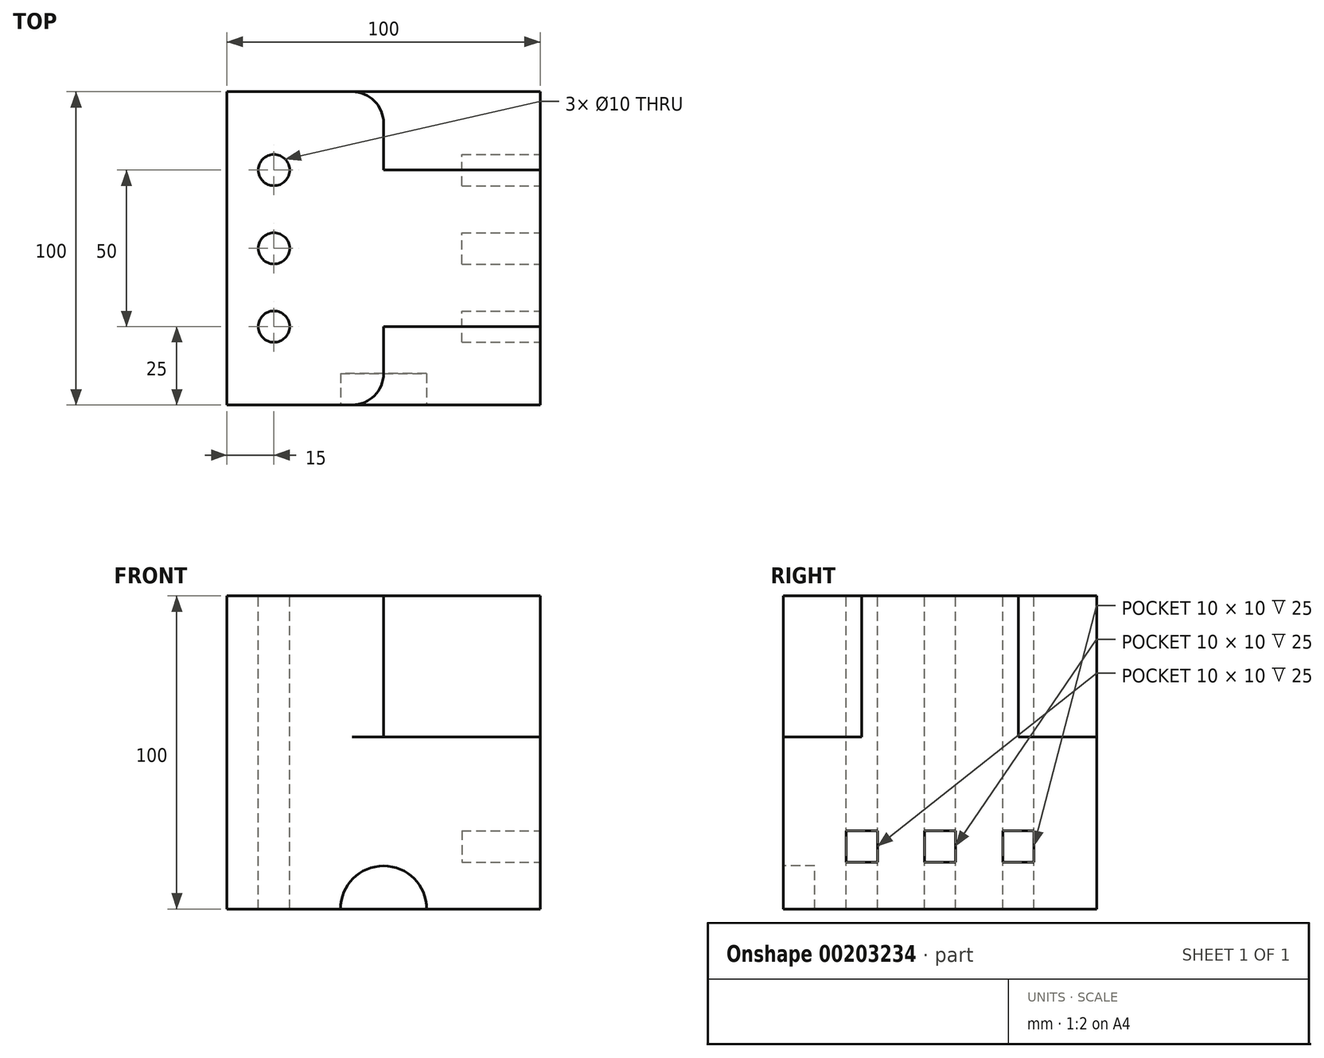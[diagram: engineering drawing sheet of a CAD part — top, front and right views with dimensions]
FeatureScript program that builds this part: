
annotation { "Feature Type Name" : "Feature", "Feature Type Description" : "" }
export const myFeature = defineFeature(function(context is Context, id is Id, definition is map)
    precondition{}
    {
        {
            var Q0;
            Q0=qCreatedBy(makeId("Front.planeOp"),FACE);
            var sketch = newSketch(context, id + "F0", { "sketchPlane" : qUnion([Q0])});
            skLineSegment(sketch, "E0", {"start": v(0, 0) * mm, "end": v(100, 0) * mm});
            skLineSegment(sketch, "E1", {"start": v(100, 0) * mm, "end": v(100, 100) * mm});
            skLineSegment(sketch, "E2", {"start": v(100, 100) * mm, "end": v(0, 100) * mm});
            skLineSegment(sketch, "E3", {"start": v(0, 100) * mm, "end": v(0, 0) * mm});
            skSolve(sketch);
        }
        {
            var Q0;
            Q0=makeQuery(id+"F0.imprint","IMPRINT",FACE,{"disambiguationData":[TD([[makeQuery(id+"F0.imprint","IMPRINT",EDGE,{"derivedFrom":sQuery(id+"F0.wireOp",EDGE,"E0")}),1.0]])]});
            extrude(context, id + "F1", {"entities" : qUnion([Q0]), "depth" : 100 * mm});
        }
        {
            var Q0;
            Q0=makeQuery(id+"F1.opExtrude","SWEPT_FACE",FACE,{"disambiguationData":[OSD([sQuery(id+"F0.wireOp",EDGE,"E2")])]});
            var sketch = newSketch(context, id + "F2", { "sketchPlane" : qUnion([Q0])});
            skLineSegment(sketch, "E4", {"start": v(100, -25) * mm, "end": v(50, -25) * mm});
            skLineSegment(sketch, "E5", {"start": v(50, -10) * mm, "end": v(50, -25) * mm});
            skLineSegment(sketch, "E6", {"start": v(50, -75) * mm, "end": v(100, -75) * mm});
            skLineSegment(sketch, "E7", {"start": v(50, -75) * mm, "end": v(50, -90) * mm});
            skLineSegment(sketch, "E8", {"start": v(0, -100) * mm, "end": v(40, -100) * mm});
            skPoint(sketch, "E9.visualSharp", {"position": v(50, -100) * mm});
            skArc(sketch, "E9.filletArc", {"start": v(40, -100) * mm, "mid": v(47.07, -97.07) * mm, "end": v(50, -90) * mm});
            skLineSegment(sketch, "E10", {"start": v(40, 0) * mm, "end": v(15.8, 0) * mm});
            skLineSegment(sketch, "E11", {"start": v(100, -25) * mm, "end": v(100, -75) * mm});
            skPoint(sketch, "E12.visualSharp", {"position": v(50, 0) * mm});
            skArc(sketch, "E12.filletArc", {"start": v(50, -10) * mm, "mid": v(47.07, -2.93) * mm, "end": v(40, 0) * mm});
            skCircle(sketch, "E13", {"center": v(15, -25) * mm, "radius": 5 * mm});
            skCircle(sketch, "E14", {"center": v(15, -50) * mm, "radius": 5 * mm});
            skCircle(sketch, "E15", {"center": v(15, -75) * mm, "radius": 5 * mm});
            skSolve(sketch);
        }
        {
            var Q0;
            Q0=makeQuery(id+"F2.imprint","IMPRINT",FACE,{"disambiguationData":[TD([[makeQuery(id+"F2.imprint","IMPRINT",EDGE,{"derivedFrom":sQuery(id+"F2.wireOp",EDGE,"E13")}),1.0]])]});
            var Q1;
            Q1=makeQuery(id+"F2.imprint","IMPRINT",FACE,{"disambiguationData":[TD([[makeQuery(id+"F2.imprint","IMPRINT",EDGE,{"derivedFrom":sQuery(id+"F2.wireOp",EDGE,"E14")}),1.0]])]});
            var Q2;
            Q2=makeQuery(id+"F2.imprint","IMPRINT",FACE,{"disambiguationData":[TD([[makeQuery(id+"F2.imprint","IMPRINT",EDGE,{"derivedFrom":sQuery(id+"F2.wireOp",EDGE,"E15")}),1.0]])]});
            var Q3;
            Q3=sQuery(id+"F2.wireOp",EDGE,"E13");
            var Q4;
            Q4=sQuery(id+"F2.wireOp",EDGE,"E14");
            var Q5;
            Q5=sQuery(id+"F2.wireOp",EDGE,"E15");
            extrude(context, id + "F3", {"entities" : qUnion([Q0, Q1, Q2]), "operationType" : NewBodyOperationType.REMOVE, "surfaceEntities" : qUnion([Q3, Q4, Q5]), "endBound" : BoundingType.THROUGH_ALL, "oppositeDirection" : true, "depth" : 25 * mm});
        }
        {
            var Q0;
            {var subQ4=sQuery(id+"F2.wireOp",EDGE,"E4");Q0=makeQuery(id+"F2.imprint","IMPRINT",FACE,{"disambiguationData":[TD([[makeQuery(id+"F2.imprint","IMPRINT",EDGE,{"derivedFrom":subQ4}),-1.0]])]});}
            var Q1;
            {var subQ5=sQuery(id+"F2.wireOp",EDGE,"E6");Q1=makeQuery(id+"F2.imprint","IMPRINT",FACE,{"disambiguationData":[TD([[makeQuery(id+"F2.imprint","IMPRINT",EDGE,{"derivedFrom":subQ5}),-1.0]])]});}
            extrude(context, id + "F4", {"entities" : qUnion([Q0, Q1]), "operationType" : NewBodyOperationType.REMOVE, "oppositeDirection" : true, "depth" : 45 * mm});
        }
        {
            var Q0;
            Q0=makeQuery(id+"F1.opExtrude","SWEPT_FACE",FACE,{"disambiguationData":[OSD([sQuery(id+"F0.wireOp",EDGE,"E1")])]});
            var sketch = newSketch(context, id + "F5", { "sketchPlane" : qUnion([Q0])});
            skLineSegment(sketch, "E16.bottom", {"start": v(-80, 25) * mm, "end": v(-70, 25) * mm});
            skLineSegment(sketch, "E16.top", {"start": v(-80, 15) * mm, "end": v(-70, 15) * mm});
            skLineSegment(sketch, "E16.left", {"start": v(-80, 25) * mm, "end": v(-80, 15) * mm});
            skLineSegment(sketch, "E16.right", {"start": v(-70, 25) * mm, "end": v(-70, 15) * mm});
            skPoint(sketch, "E16.middle", {"position": v(-75, 20) * mm});
            skLineSegment(sketch, "E17.bottom", {"start": v(-55, 25) * mm, "end": v(-45, 25) * mm});
            skLineSegment(sketch, "E17.top", {"start": v(-55, 15) * mm, "end": v(-45, 15) * mm});
            skLineSegment(sketch, "E17.left", {"start": v(-55, 25) * mm, "end": v(-55, 15) * mm});
            skLineSegment(sketch, "E17.right", {"start": v(-45, 25) * mm, "end": v(-45, 15) * mm});
            skPoint(sketch, "E17.middle", {"position": v(-50, 20) * mm});
            skLineSegment(sketch, "E18.bottom", {"start": v(-30, 25) * mm, "end": v(-20, 25) * mm});
            skLineSegment(sketch, "E18.top", {"start": v(-30, 15) * mm, "end": v(-20, 15) * mm});
            skLineSegment(sketch, "E18.left", {"start": v(-30, 25) * mm, "end": v(-30, 15) * mm});
            skLineSegment(sketch, "E18.right", {"start": v(-20, 25) * mm, "end": v(-20, 15) * mm});
            skPoint(sketch, "E18.middle", {"position": v(-25, 20) * mm});
            skSolve(sketch);
        }
        {
            var Q0;
            Q0=makeQuery(id+"F5.imprint","IMPRINT",FACE,{"disambiguationData":[TD([[makeQuery(id+"F5.imprint","IMPRINT",EDGE,{"derivedFrom":sQuery(id+"F5.wireOp",EDGE,"E16.bottom")}),-1.0]])]});
            var Q1;
            Q1=makeQuery(id+"F5.imprint","IMPRINT",FACE,{"disambiguationData":[TD([[makeQuery(id+"F5.imprint","IMPRINT",EDGE,{"derivedFrom":sQuery(id+"F5.wireOp",EDGE,"E17.bottom")}),-1.0]])]});
            var Q2;
            Q2=makeQuery(id+"F5.imprint","IMPRINT",FACE,{"disambiguationData":[TD([[makeQuery(id+"F5.imprint","IMPRINT",EDGE,{"derivedFrom":sQuery(id+"F5.wireOp",EDGE,"E18.bottom")}),-1.0]])]});
            extrude(context, id + "F6", {"entities" : qUnion([Q0, Q1, Q2]), "operationType" : NewBodyOperationType.REMOVE, "oppositeDirection" : true, "depth" : 25 * mm});
        }
        {
            var Q0;
            Q0=makeQuery(id+"F1.opExtrude","CAP_FACE",FACE,{"disambiguationData":[OSD([sQuery(id+"F0.wireOp",EDGE,"E0"),sQuery(id+"F0.wireOp",EDGE,"E1"),sQuery(id+"F0.wireOp",EDGE,"E2"),sQuery(id+"F0.wireOp",EDGE,"E3")])],"isStart":false});
            var sketch = newSketch(context, id + "F7", { "sketchPlane" : qUnion([Q0])});
            skArc(sketch, "E19", {"start": v(63.75, 0) * mm, "mid": v(50, 13.75) * mm, "end": v(36.25, 0) * mm});
            skSolve(sketch);
        }
        {
            var Q0;
            {var subQ0=sQuery(id+"F7.wireOp",EDGE,"E19");Q0=makeQuery(id+"F7.imprint","IMPRINT",FACE,{"disambiguationData":[TD([[makeQuery(id+"F7.imprint","IMPRINT",EDGE,{"derivedFrom":subQ0}),1.0]])]});}
            extrude(context, id + "F8", {"entities" : qUnion([Q0]), "operationType" : NewBodyOperationType.REMOVE, "oppositeDirection" : true, "depth" : 10 * mm});
        }
    });
